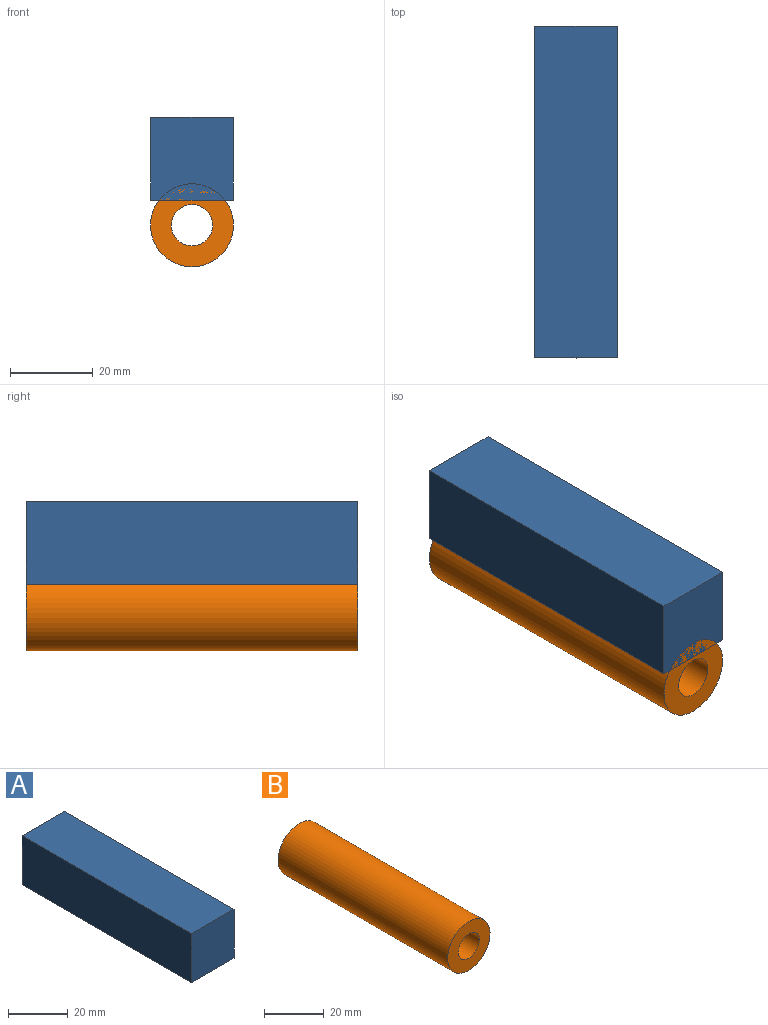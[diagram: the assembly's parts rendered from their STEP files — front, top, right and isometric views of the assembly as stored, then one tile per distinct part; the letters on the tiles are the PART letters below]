
ASSEMBLY  parts=2 mates=1
PART A: 6 faces, bbox 20x80x20 mm
  f0: plane 80x20mm, normal (-1,0,0), area 1600mm2, adj f1,f3,f4,f5
  f1: plane 20x20mm, normal (0,-1,0), area 400mm2, adj f0,f2,f4,f5
  f2: plane 80x20mm, normal (1,0,0), area 1600mm2, adj f1,f3,f4,f5
  f3: plane 20x20mm, normal (0,1,0), area 400mm2, adj f0,f2,f4,f5
  f4: plane 80x20mm, normal (0,0,1), area 1600mm2, adj f0,f1,f2,f3
  f5: plane 80x20mm, normal (0,0,-1), area 1600mm2, adj f0,f1,f2,f3
PART B: 4 faces, bbox 20x80x20 mm
  f0: cylinder r=10mm len=80mm, axis (0,1,0), area 5026.5mm2, adj f1,f2
  f1: plane 20x20mm, normal (0,-1,0), area 235.6mm2, adj f0,f3
  f2: plane 20x20mm, normal (0,1,0), area 235.6mm2, adj f0,f3
  f3: cylinder r=5mm len=80mm, axis (0,-1,0), area 2513.3mm2, adj f1,f2
PLACE A t=(-5.42,-59.17,-26.67)mm
PLACE B t=(4.58,20.83,-32.72)mm
MATE planar A.f1 <-> B.f0  axis (0,-1,0) through (4.58,-59.17,-16.67)mm
